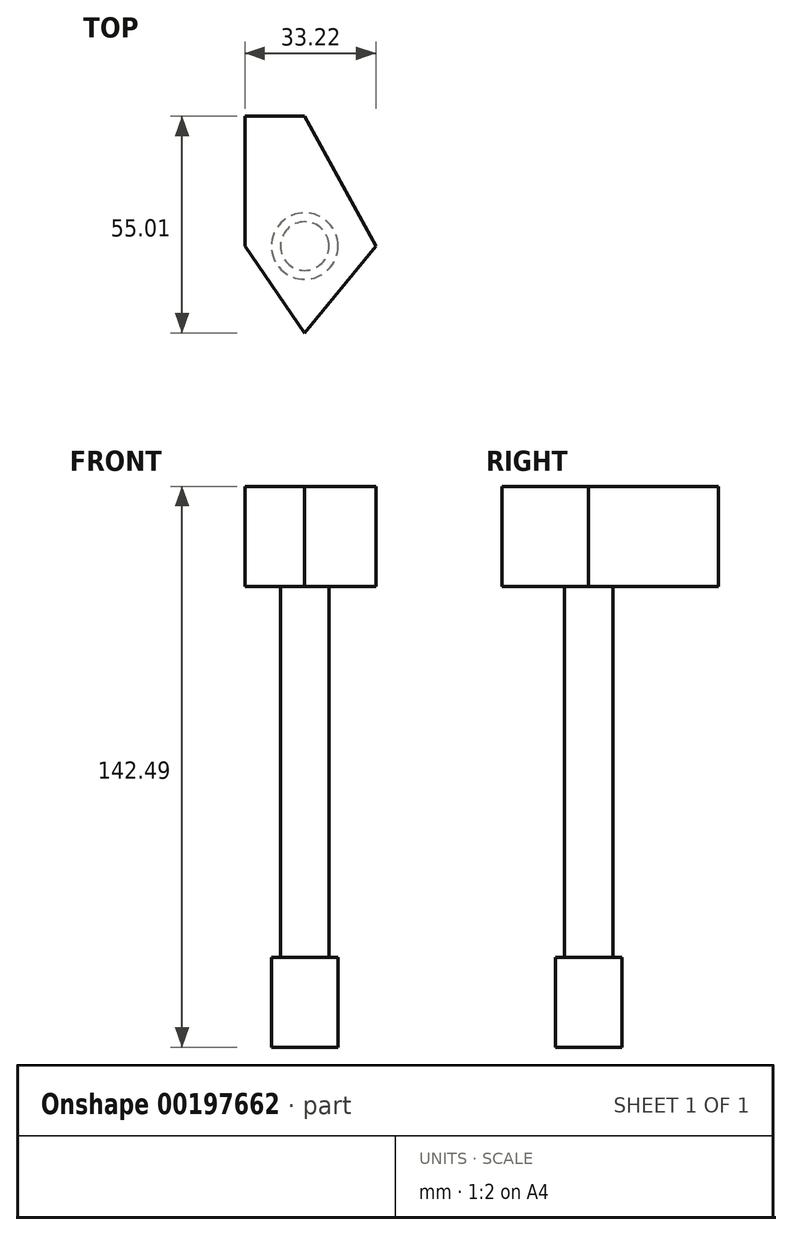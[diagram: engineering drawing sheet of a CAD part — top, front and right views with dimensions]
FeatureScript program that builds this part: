
annotation { "Feature Type Name" : "Feature", "Feature Type Description" : "" }
export const myFeature = defineFeature(function(context is Context, id is Id, definition is map)
    precondition{}
    {
        {
            var Q0;
            Q0=qCreatedBy(makeId("Top.planeOp"),FACE);
            var sketch = newSketch(context, id + "F0", { "sketchPlane" : qUnion([Q0])});
            skCircle(sketch, "E0", {"center": v(0, 0) * mm, "radius": 6.17 * mm});
            skSolve(sketch);
        }
        {
            var Q0;
            Q0 = qSketchRegion(id + "F0", true);
            extrude(context, id + "F1", {"entities" : qUnion([Q0]), "depth" : 117.1 * mm});
        }
        {
            var Q0;
            Q0=qCreatedBy(makeId("Top.planeOp"),FACE);
            var sketch = newSketch(context, id + "F2", { "sketchPlane" : qUnion([Q0])});
            skCircle(sketch, "E1", {"center": v(0, 0) * mm, "radius": 8.45 * mm});
            skSolve(sketch);
        }
        {
            var Q0;
            Q0 = qSketchRegion(id + "F2", true);
            extrude(context, id + "F3", {"entities" : qUnion([Q0]), "operationType" : NewBodyOperationType.ADD, "depth" : 22.86 * mm});
        }
        {
            var Q0;
            Q0=makeQuery(id+"F1.opExtrude","CAP_FACE",FACE,{"disambiguationData":[OSD([sQuery(id+"F0.wireOp",EDGE,"E0")])],"isStart":false});
            var sketch = newSketch(context, id + "F4", { "sketchPlane" : qUnion([Q0])});
            skLineSegment(sketch, "E2", {"start": v(0, 0) * mm, "end": v(0, 32.96) * mm});
            skLineSegment(sketch, "E3", {"start": v(0, 32.96) * mm, "end": v(-15.15, 32.96) * mm});
            skLineSegment(sketch, "E4", {"start": v(-15.15, 32.96) * mm, "end": v(-15.15, 0) * mm});
            skLineSegment(sketch, "E5", {"start": v(-15.15, 0) * mm, "end": v(0, 0) * mm});
            skLineSegment(sketch, "E6", {"start": v(0, 0) * mm, "end": v(18.07, 0) * mm});
            skLineSegment(sketch, "E7", {"start": v(18.07, 0) * mm, "end": v(0, 32.96) * mm});
            skLineSegment(sketch, "E8", {"start": v(18.07, 0) * mm, "end": v(0, -22.05) * mm});
            skLineSegment(sketch, "E9", {"start": v(0, -22.05) * mm, "end": v(-15.15, 0) * mm});
            skLineSegment(sketch, "E10", {"start": v(0, -22.05) * mm, "end": v(0, 0) * mm});
            skLineSegment(sketch, "E11", {"start": v(-15.15, 0) * mm, "end": v(0, 32.96) * mm});
            skSolve(sketch);
        }
        {
            var Q0;
            Q0 = qSketchRegion(id + "F4", true);
            extrude(context, id + "F5", {"entities" : qUnion([Q0]), "operationType" : NewBodyOperationType.ADD, "depth" : 25.4 * mm});
        }
    });
